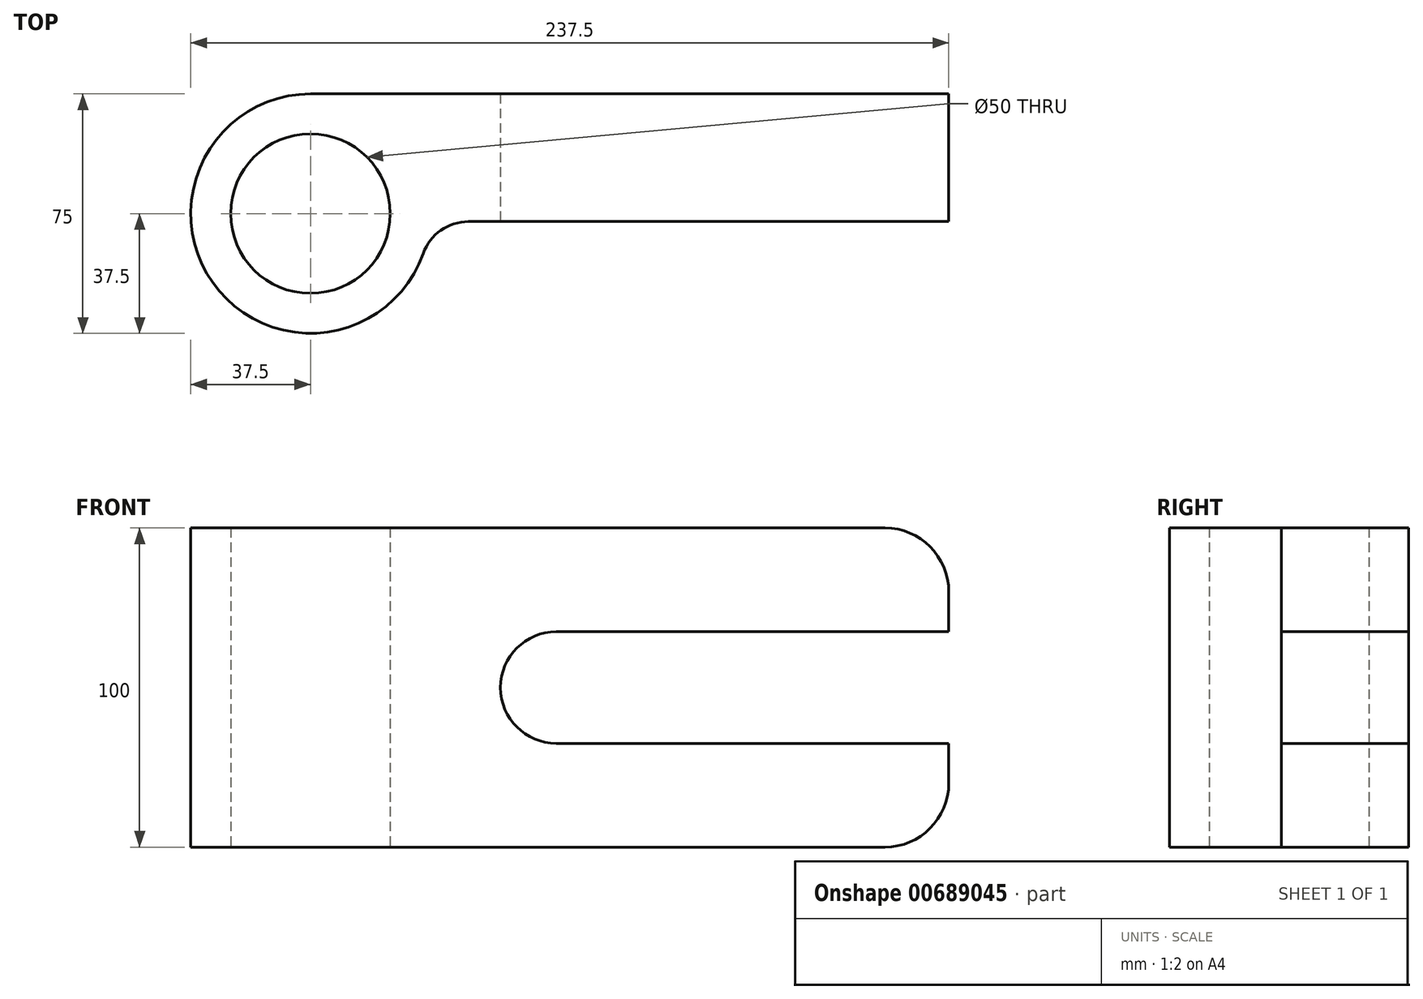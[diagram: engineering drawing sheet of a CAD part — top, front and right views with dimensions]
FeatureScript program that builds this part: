
annotation { "Feature Type Name" : "Feature", "Feature Type Description" : "" }
export const myFeature = defineFeature(function(context is Context, id is Id, definition is map)
    precondition{}
    {
        {
            var Q0;
            Q0=qCreatedBy(makeId("Top.planeOp"),FACE);
            var sketch = newSketch(context, id + "F0", { "sketchPlane" : qUnion([Q0])});
            skCircle(sketch, "E0", {"center": v(0, 0) * mm, "radius": 25 * mm});
            skArc(sketch, "E1", {"start": v(0, 37.5) * mm, "mid": v(-30.62, -21.65) * mm, "end": v(35.36, -12.5) * mm});
            skLineSegment(sketch, "E2", {"start": v(0, 37.5) * mm, "end": v(200, 37.5) * mm});
            skLineSegment(sketch, "E3", {"start": v(200, 37.5) * mm, "end": v(200, -2.5) * mm});
            skLineSegment(sketch, "E4", {"start": v(200, -2.5) * mm, "end": v(49.5, -2.5) * mm});
            skPoint(sketch, "E5.visualSharp", {"position": v(37.42, -2.5) * mm});
            skArc(sketch, "E5.filletArc", {"start": v(49.5, -2.5) * mm, "mid": v(40.84, -5.25) * mm, "end": v(35.36, -12.5) * mm});
            skSolve(sketch);
        }
        {
            var Q0;
            Q0 = qSketchRegion(id + "F0", true);
            extrude(context, id + "F1", {"entities" : qUnion([Q0]), "depth" : 100 * mm, "offsetDistance" : 25 * mm});
        }
        {
            var Q0;
            Q0=makeQuery(id+"F1.opExtrude","SWEPT_FACE",FACE,{"disambiguationData":[OSD([sQuery(id+"F0.wireOp",EDGE,"E4")])]});
            var sketch = newSketch(context, id + "F2", { "sketchPlane" : qUnion([Q0])});
            skArc(sketch, "E6", {"start": v(77.04, 67.5) * mm, "mid": v(59.54, 50) * mm, "end": v(77.04, 32.5) * mm});
            skPoint(sketch, "E6.centerSnap0", {"position": v(200, 50) * mm});
            skLineSegment(sketch, "E7", {"start": v(77.04, 67.5) * mm, "end": v(200, 67.5) * mm});
            skLineSegment(sketch, "E8", {"start": v(77.04, 32.5) * mm, "end": v(200, 32.5) * mm});
            skSolve(sketch);
        }
        {
            var Q0;
            Q0 = qSketchRegion(id + "F2", true);
            var Q1;
            Q1=makeQuery(id+"F2.imprint","IMPRINT",FACE,{"disambiguationData":[TD([[makeQuery(id+"F2.imprint","IMPRINT",EDGE,{"derivedFrom":sQuery(id+"F2.wireOp",EDGE,"E6")}),1.0]])]});
            extrude(context, id + "F3", {"entities" : qUnion([Q0, Q1]), "operationType" : NewBodyOperationType.REMOVE, "oppositeDirection" : true, "depth" : 50 * mm, "offsetDistance" : 25 * mm});
        }
        {
            var Q0;
            Q0=makeQuery(id+"F1.opExtrude","CAP_EDGE",EDGE,{"disambiguationData":[OSD([sQuery(id+"F0.wireOp",EDGE,"E3")])],"isStart":false});
            var Q1;
            Q1=makeQuery(id+"F1.opExtrude","CAP_EDGE",EDGE,{"disambiguationData":[OSD([sQuery(id+"F0.wireOp",EDGE,"E3")])],"isStart":true});
            fillet(context, id + "F4", {"entities" : qUnion([Q0, Q1]), "radius" : 20 * mm, "tangentPropagation" : true, "allowEdgeOverflow" : false});
        }
    });
